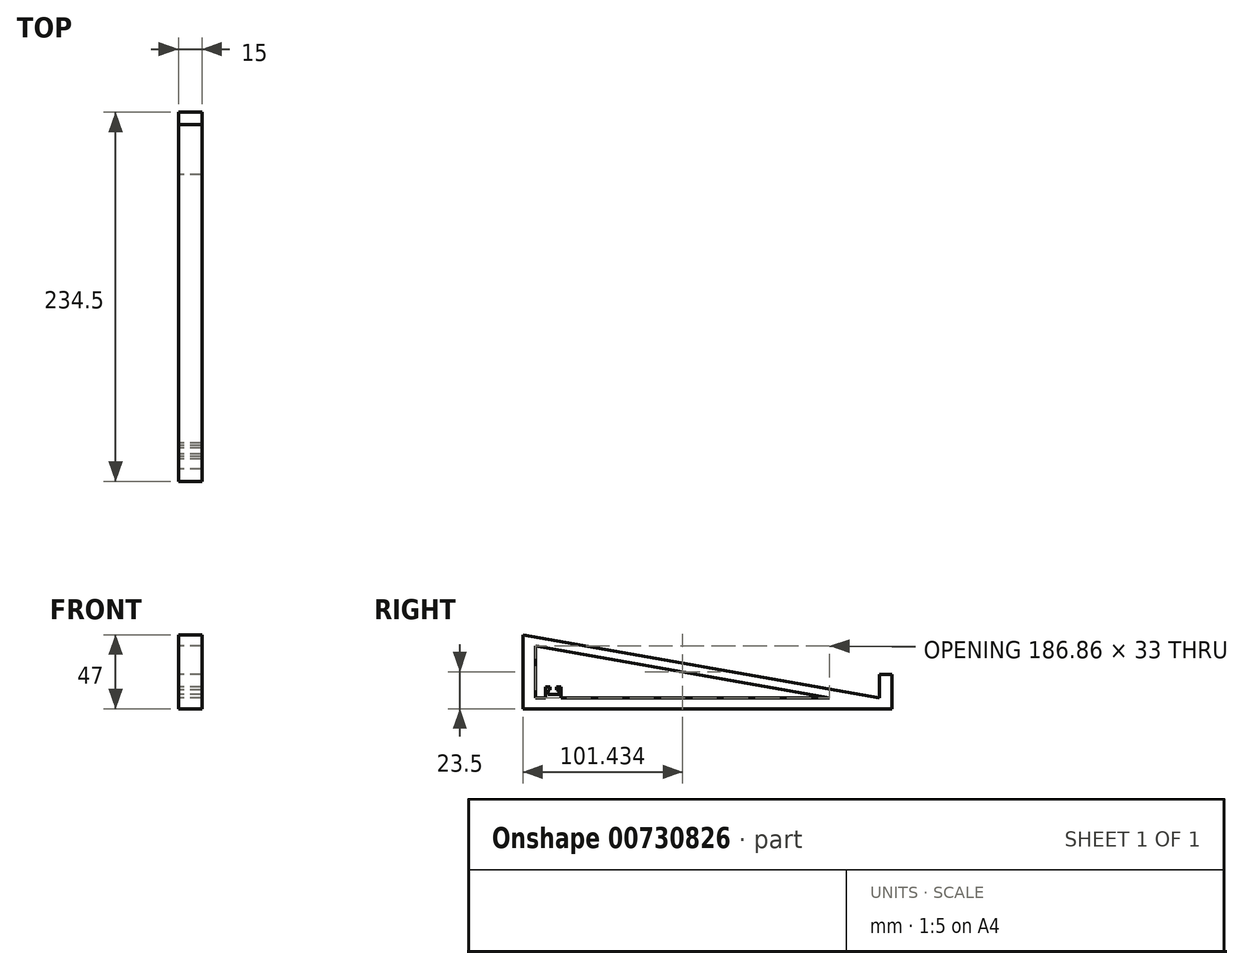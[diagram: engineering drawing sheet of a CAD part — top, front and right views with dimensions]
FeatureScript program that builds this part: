
annotation { "Feature Type Name" : "Feature", "Feature Type Description" : "" }
export const myFeature = defineFeature(function(context is Context, id is Id, definition is map)
    precondition{}
    {
        {
            var Q0;
            Q0=qCreatedBy(makeId("Right.planeOp"),FACE);
            var sketch = newSketch(context, id + "F0", { "sketchPlane" : qUnion([Q0])});
            skLineSegment(sketch, "E0", {"start": v(96.85, 0) * mm, "end": v(96.85, 22) * mm});
            skLineSegment(sketch, "E1", {"start": v(96.85, 22) * mm, "end": v(88.85, 22) * mm});
            skLineSegment(sketch, "E2", {"start": v(88.85, 22) * mm, "end": v(88.85, 7) * mm});
            skLineSegment(sketch, "E3", {"start": v(88.85, 7) * mm, "end": v(-137.65, 47) * mm});
            skLineSegment(sketch, "E4", {"start": v(-137.65, 47) * mm, "end": v(-137.65, 0) * mm});
            skLineSegment(sketch, "E5", {"start": v(-137.65, 0) * mm, "end": v(-129.65, 0) * mm});
            skLineSegment(sketch, "E6", {"start": v(-129.65, 0) * mm, "end": v(-129.65, 40) * mm});
            skLineSegment(sketch, "E7", {"start": v(-129.65, 40) * mm, "end": v(96.85, 0) * mm});
            skLineSegment(sketch, "E8", {"start": v(-129.65, 0) * mm, "end": v(96.85, 0) * mm});
            skLineSegment(sketch, "E9", {"start": v(-129.65, 7) * mm, "end": v(88.85, 7) * mm});
            skLineSegment(sketch, "E10", {"start": v(-123.3, 7) * mm, "end": v(-123.3, 14) * mm});
            skLineSegment(sketch, "E11", {"start": v(-123.3, 14) * mm, "end": v(-120.3, 14) * mm});
            skLineSegment(sketch, "E12", {"start": v(-120.3, 14) * mm, "end": v(-120.3, 12) * mm});
            skLineSegment(sketch, "E13", {"start": v(-120.3, 12) * mm, "end": v(-121.8, 12) * mm});
            skLineSegment(sketch, "E14", {"start": v(-121.8, 12) * mm, "end": v(-121.8, 9) * mm});
            skLineSegment(sketch, "E15", {"start": v(-121.8, 9) * mm, "end": v(-114.8, 9) * mm});
            skLineSegment(sketch, "E16", {"start": v(-114.8, 9) * mm, "end": v(-114.8, 12) * mm});
            skLineSegment(sketch, "E17", {"start": v(-114.8, 12) * mm, "end": v(-116.3, 12) * mm});
            skLineSegment(sketch, "E18", {"start": v(-116.3, 12) * mm, "end": v(-116.3, 14) * mm});
            skLineSegment(sketch, "E19", {"start": v(-116.3, 14) * mm, "end": v(-113.3, 14) * mm});
            skLineSegment(sketch, "E20", {"start": v(-113.3, 14) * mm, "end": v(-113.3, 7) * mm});
            skLineSegment(sketch, "E21", {"start": v(-113.3, 7) * mm, "end": v(-113.3, 14) * mm});
            skLineSegment(sketch, "E22", {"start": v(-113.3, 14) * mm, "end": v(-110.3, 14) * mm});
            skLineSegment(sketch, "E23", {"start": v(-110.3, 14) * mm, "end": v(-110.3, 12) * mm});
            skLineSegment(sketch, "E24", {"start": v(-110.3, 12) * mm, "end": v(-111.8, 12) * mm});
            skLineSegment(sketch, "E25", {"start": v(-111.8, 12) * mm, "end": v(-111.8, 9) * mm});
            skLineSegment(sketch, "E26", {"start": v(-111.8, 9) * mm, "end": v(-104.8, 9) * mm});
            skLineSegment(sketch, "E27", {"start": v(-104.8, 9) * mm, "end": v(-104.8, 12) * mm});
            skLineSegment(sketch, "E28", {"start": v(-104.8, 12) * mm, "end": v(-106.3, 12) * mm});
            skLineSegment(sketch, "E29", {"start": v(-106.3, 12) * mm, "end": v(-106.3, 14) * mm});
            skLineSegment(sketch, "E30", {"start": v(-106.3, 14) * mm, "end": v(-103.3, 14) * mm});
            skLineSegment(sketch, "E31", {"start": v(-103.3, 14) * mm, "end": v(-103.3, 7) * mm});
            skLineSegment(sketch, "E32", {"start": v(-103.3, 7) * mm, "end": v(-103.3, 14) * mm});
            skLineSegment(sketch, "E33", {"start": v(-103.3, 14) * mm, "end": v(-100.3, 14) * mm});
            skLineSegment(sketch, "E34", {"start": v(-100.3, 14) * mm, "end": v(-100.3, 12) * mm});
            skLineSegment(sketch, "E35", {"start": v(-100.3, 12) * mm, "end": v(-101.8, 12) * mm});
            skLineSegment(sketch, "E36", {"start": v(-101.8, 12) * mm, "end": v(-101.8, 9) * mm});
            skLineSegment(sketch, "E37", {"start": v(-101.8, 9) * mm, "end": v(-94.8, 9) * mm});
            skLineSegment(sketch, "E38", {"start": v(-94.8, 9) * mm, "end": v(-94.8, 12) * mm});
            skLineSegment(sketch, "E39", {"start": v(-94.8, 12) * mm, "end": v(-96.3, 12) * mm});
            skLineSegment(sketch, "E40", {"start": v(-96.3, 12) * mm, "end": v(-96.3, 14) * mm});
            skLineSegment(sketch, "E41", {"start": v(-96.3, 14) * mm, "end": v(-93.3, 14) * mm});
            skLineSegment(sketch, "E42", {"start": v(-93.3, 14) * mm, "end": v(-93.3, 7) * mm});
            skSolve(sketch);
        }
        {
            var Q0;
            Q0 = qSketchRegion(id + "F0", true);
            var Q1;
            {var subQ0=sQuery(id+"F0.wireOp",EDGE,"E10");Q1=makeQuery(id+"F0.imprint","IMPRINT",FACE,{"disambiguationData":[TD([[makeQuery(id+"F0.imprint","IMPRINT",EDGE,{"derivedFrom":subQ0}),-1.0]])]});}
            var Q2;
            {var subQ0=sQuery(id+"F0.wireOp",EDGE,"E21");Q2=makeQuery(id+"F0.imprint","IMPRINT",FACE,{"disambiguationData":[TD([[makeQuery(id+"F0.imprint","IMPRINT",EDGE,{"derivedFrom":subQ0}),-1.0]])]});}
            var Q3;
            {var subQ0=sQuery(id+"F0.wireOp",EDGE,"E32");Q3=makeQuery(id+"F0.imprint","IMPRINT",FACE,{"disambiguationData":[TD([[makeQuery(id+"F0.imprint","IMPRINT",EDGE,{"derivedFrom":subQ0}),-1.0]])]});}
            extrude(context, id + "F1", {"entities" : qUnion([Q0, Q1, Q2, Q3]), "depth" : 15 * mm, "offsetDistance" : 25 * mm});
        }
    });
